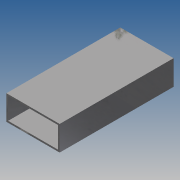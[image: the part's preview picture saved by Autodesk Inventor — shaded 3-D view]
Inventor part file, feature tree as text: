
AUTODESK INVENTOR PART (.ipt)
format: ipt  version: 2013 SP2 (Build 170200200, 200)  size: 79,872 bytes
history: native  units: in
note: dims shown in document units (in); Inventor stores cm internally (conversion verified against a paired STEP export)
features: extrude x1, sketch x1
ambient origin geometry x8: Origin, YZ Plane, XZ Plane, XY Plane, X Axis, Y Axis, Z Axis, Center Point
bodies: Solid1 (feature_tree)
feature tree (2):
  extrude  "Extrusion1"  Depth=1.5in
  sketch  "Sketch1"  dims[d0=3.5in d1=1.5in d2=0.12in d3=8.0in d4=0.0in]
